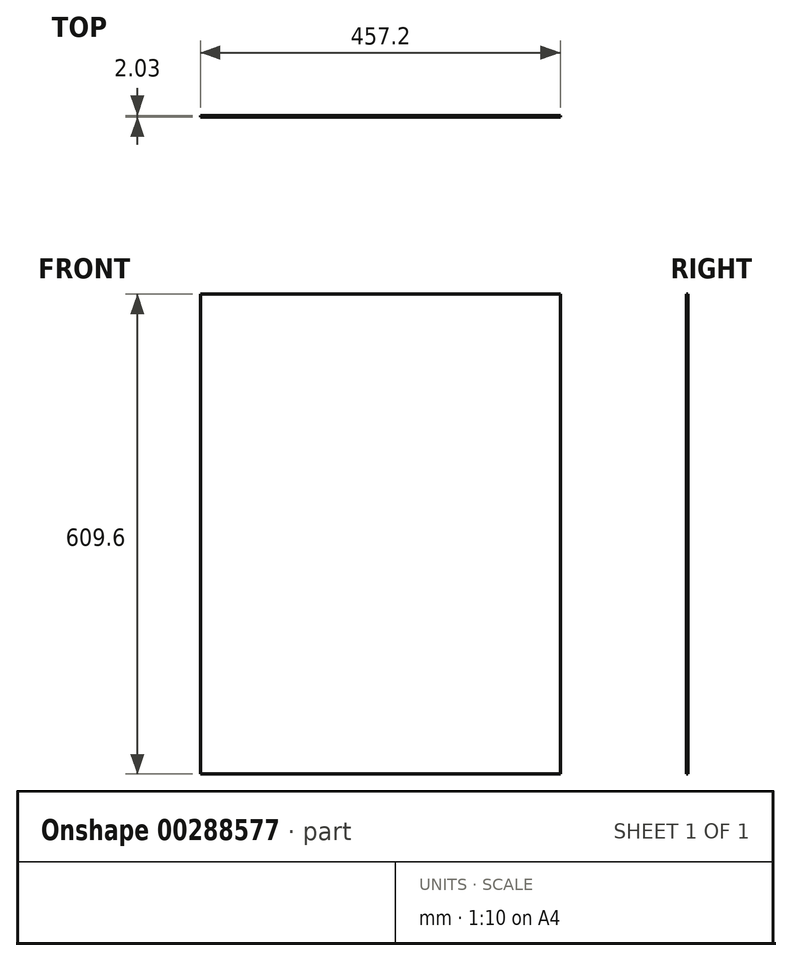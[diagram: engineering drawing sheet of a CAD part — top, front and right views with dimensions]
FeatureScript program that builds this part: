
annotation { "Feature Type Name" : "Feature", "Feature Type Description" : "" }
export const myFeature = defineFeature(function(context is Context, id is Id, definition is map)
    precondition{}
    {
        {
            var Q0;
            Q0=qCreatedBy(makeId("Front.planeOp"),FACE);
            var sketch = newSketch(context, id + "F0", { "sketchPlane" : qUnion([Q0])});
            skLineSegment(sketch, "E0.bottom", {"start": v(228.6, 304.8) * mm, "end": v(-228.6, 304.8) * mm});
            skLineSegment(sketch, "E0.top", {"start": v(228.6, -304.8) * mm, "end": v(-228.6, -304.8) * mm});
            skLineSegment(sketch, "E0.left", {"start": v(228.6, 304.8) * mm, "end": v(228.6, -304.8) * mm});
            skLineSegment(sketch, "E0.right", {"start": v(-228.6, 304.8) * mm, "end": v(-228.6, -304.8) * mm});
            skPoint(sketch, "E0.middle", {"position": v(0, 0) * mm});
            skSolve(sketch);
        }
        {
            var Q0;
            Q0 = qSketchRegion(id + "F0", true);
            extrude(context, id + "F1", {"entities" : qUnion([Q0]), "depth" : 2.03 * mm});
        }
    });
